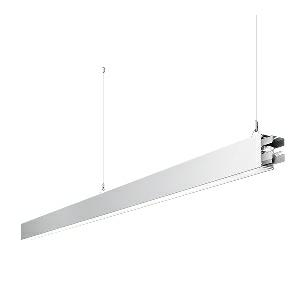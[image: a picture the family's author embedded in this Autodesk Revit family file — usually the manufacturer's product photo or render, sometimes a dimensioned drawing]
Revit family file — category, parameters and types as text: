
# Revit family: dotoo_line_-_dlp_3000_840_d_mid_00805786_7357
name_source: partatom
category: Lighting Fixtures
units: mm (PartAtom-declared; Revit-internal decimal feet)

## family parameters
Cut with Voids When Loaded = No
Host = Face
Light Source = No
Part Type = Normal
Room Calculation Point = No
Round Connector Dimension = Use Diameter
Shared = No

## types (1)
- DOTOO.line - DLP 3000/840/D MID (1 x LED, 2750 lm, 4000K)
    Apparent Load = 26 VA
    Approval mark = CE
    CIE Flux Codes = 67 91 98 100 100
    Color Rendering = 80-89
    Color Temperature = 4000K
    Control Gear = Electronic ballast
    Default Elevation = 1800 mm
    Description = DLP 3000/840/D|Suspended luminaire|light source: LED|connected load: 220-240 V, 50/60 Hz|Power consumption: approx. 26 W|standby: approx. 0,15|luminous flux: 2750 lm|luminous efficacy: 105 lm/W|light distribution: Direct|direct ratio: approx. 100 %|colour temperature: Cold white, ca. 4000 K|color rendering index (CRI): >= 80|chromaticity tolerance:  3 SDCM|System of protection: IP 40|technology: Continuously dimmable|luminaire body|material: Sectional aluminium|colour: White|lamp cover: Acrylic (PMMA), Clear|mains lead: 1,0 m With free stranded wires|Fastening: Steel cable 0.3 - 0.7 m|glare control: Prism aperture|luminance(L65): <= 3000 cd/m|unified glare rating(4H 8H): <=  19|special features: DALI Load 1x, TouchDIM - dimming via standard switch, Through-wired, up to 18 m on one mains connection, Flicker-free, Suitable as emergency lighting, Mechanical and electrical connection of the individual modules without tools|
    Frequency = 50 Hz
    Height = 110 mm
    Lamp = 1 x LED
    Lamp Light Flux = 2750 lm
    Lamp count = 1
    Length = 2244 mm
    Luminous efficacy = 106 lm/W
    Manufacturer = Waldmann
    ModVariant = No
    Model = 00805786
    Mounting Place = Ceiling
    Mounting Type = Pendant
    Number of Poles = 1
    OnlyDefault = Yes
    Power Factor = 1
    Product Name = DOTOO.line - DLP 3000/840/D MID
    Product group = Suspended luminaire
    ProductGroupID = 9
    Protection Class = Protection class I
    Protection Degree = IP 40
    RLX_Detail_Level = 1
    RLX_Emergency_Light_Flux = 0 lm
    RLX_Emergency_Type = 0
    RLX_Emergency_Type_DB = No
    RlxData = <blob elided: 22253 chars, md5=647c9cac>
    Socket = socket
    Standby Power = 0 W
    System Light Flux = 2750 lm
    System Power = 26 W
    Type Comments = Product without accessories
    Type Image = 113314000-00692606.jpg
    URL = http://relux.com
    VarID = ---
    Voltage = 230 V
    Voltage Range = 220-240 V
    Weight = 0.00 kg
    Width = 60 mm  [stored 0.19685 ft]

note: [stored X ft] marks values corroborated as IEEE doubles in the binary element streams (Revit-internal decimal feet)

## geometry (parser evidence)
native form markers: Blend x4, Sweep x11
no freeform markers — native parametric forms only
